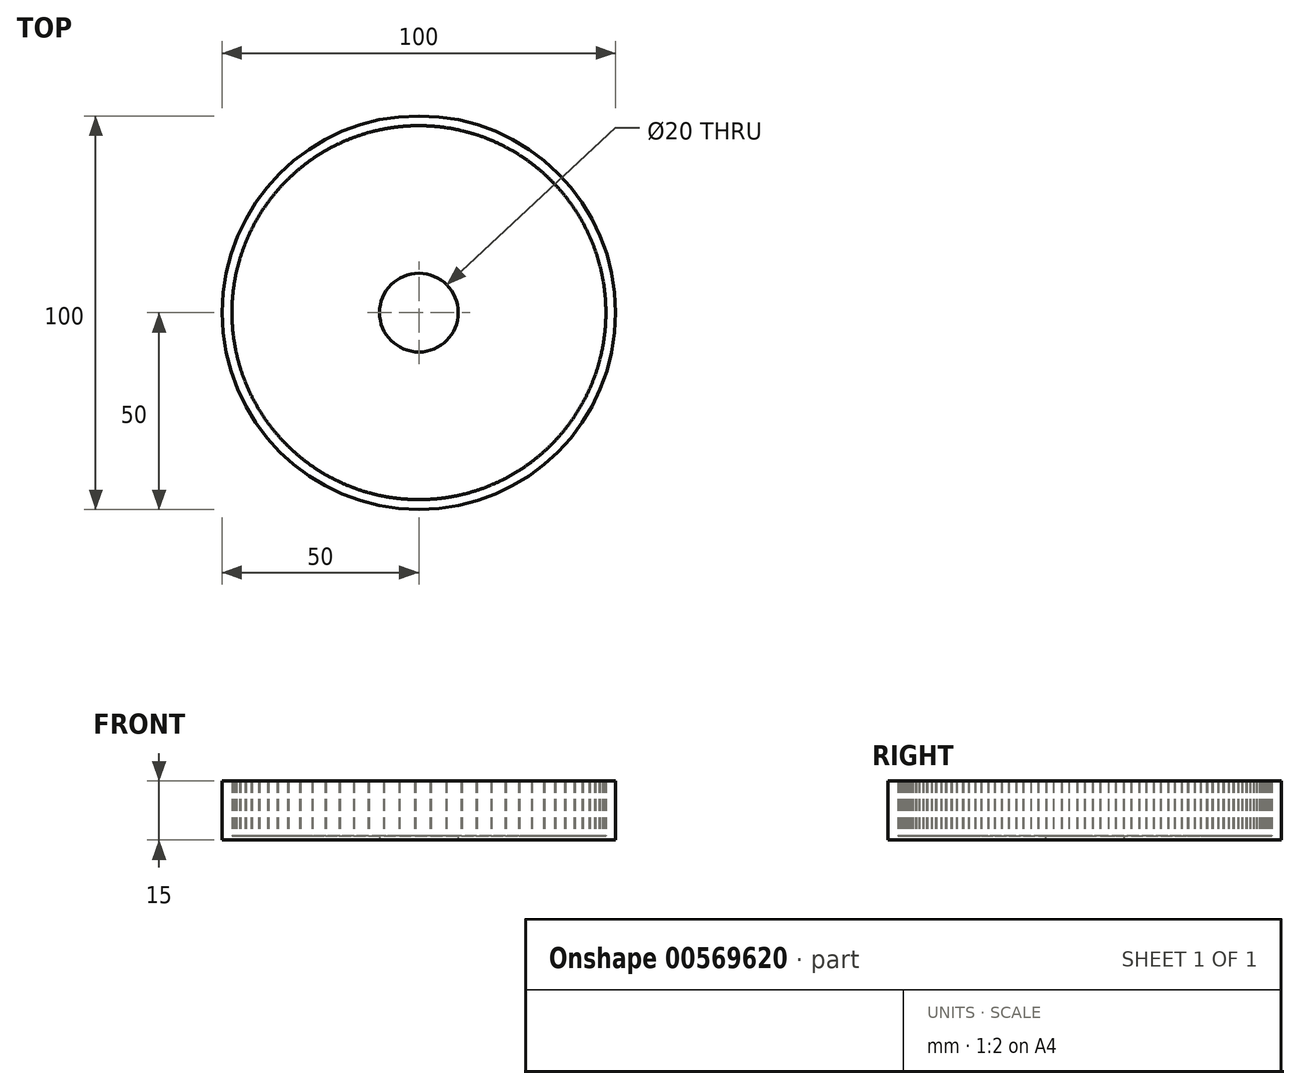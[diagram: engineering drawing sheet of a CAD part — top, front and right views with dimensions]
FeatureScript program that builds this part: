
annotation { "Feature Type Name" : "Feature", "Feature Type Description" : "" }
export const myFeature = defineFeature(function(context is Context, id is Id, definition is map)
    precondition{}
    {
        {
            var Q0;
            Q0=qCreatedBy(makeId("Top.planeOp"),FACE);
            var sketch = newSketch(context, id + "F0", { "sketchPlane" : qUnion([Q0])});
            skCircle(sketch, "E0", {"center": v(0, 0) * mm, "radius": 50 * mm});
            skCircle(sketch, "E1", {"center": v(0, 0) * mm, "radius": 10 * mm});
            skCircle(sketch, "E2", {"center": v(0, 0) * mm, "radius": 47.5 * mm});
            skLineSegment(sketch, "E3", {"start": v(47.5, 0) * mm, "end": v(47.3, -0.05) * mm});
            skLineSegment(sketch, "E4", {"start": v(47.3, -0.05) * mm, "end": v(47.5, -0.1) * mm});
            skLineSegment(sketch, "E5.1.0", {"start": v(47.33, 3.97) * mm, "end": v(47.14, 3.9) * mm});
            skLineSegment(sketch, "E5.1.1", {"start": v(47.14, 3.9) * mm, "end": v(47.34, 3.88) * mm});
            skLineSegment(sketch, "E5.2.0", {"start": v(46.83, 7.92) * mm, "end": v(46.65, 7.84) * mm});
            skLineSegment(sketch, "E5.2.1", {"start": v(46.65, 7.84) * mm, "end": v(46.85, 7.82) * mm});
            skLineSegment(sketch, "E6.2.3.0", {"start": v(46, 11.81) * mm, "end": v(45.83, 11.71) * mm});
            skLineSegment(sketch, "E6.3.3.0", {"start": v(45.83, 11.71) * mm, "end": v(46.03, 11.72) * mm});
            skLineSegment(sketch, "E6.2.4.0", {"start": v(44.86, 15.62) * mm, "end": v(44.69, 15.5) * mm});
            skLineSegment(sketch, "E6.3.4.0", {"start": v(44.69, 15.5) * mm, "end": v(44.9, 15.53) * mm});
            skLineSegment(sketch, "E6.2.5.0", {"start": v(43.4, 19.32) * mm, "end": v(43.23, 19.2) * mm});
            skLineSegment(sketch, "E6.3.5.0", {"start": v(43.23, 19.2) * mm, "end": v(43.43, 19.23) * mm});
            skLineSegment(sketch, "E6.2.6.0", {"start": v(41.62, 22.88) * mm, "end": v(41.47, 22.74) * mm});
            skLineSegment(sketch, "E6.3.6.0", {"start": v(41.47, 22.74) * mm, "end": v(41.67, 22.8) * mm});
            skLineSegment(sketch, "E6.2.7.0", {"start": v(39.56, 26.29) * mm, "end": v(39.42, 26.13) * mm});
            skLineSegment(sketch, "E6.3.7.0", {"start": v(39.42, 26.13) * mm, "end": v(39.62, 26.2) * mm});
            skLineSegment(sketch, "E6.2.8.0", {"start": v(37.23, 29.5) * mm, "end": v(37.1, 29.34) * mm});
            skLineSegment(sketch, "E6.3.8.0", {"start": v(37.1, 29.34) * mm, "end": v(37.29, 29.43) * mm});
            skLineSegment(sketch, "E6.2.9.0", {"start": v(34.63, 32.52) * mm, "end": v(34.51, 32.34) * mm});
            skLineSegment(sketch, "E6.3.9.0", {"start": v(34.51, 32.34) * mm, "end": v(34.7, 32.44) * mm});
            skLineSegment(sketch, "E6.2.10.0", {"start": v(31.78, 35.3) * mm, "end": v(31.69, 35.12) * mm});
            skLineSegment(sketch, "E6.3.10.0", {"start": v(31.69, 35.12) * mm, "end": v(31.86, 35.23) * mm});
            skLineSegment(sketch, "E6.2.11.0", {"start": v(28.72, 37.84) * mm, "end": v(28.64, 37.65) * mm});
            skLineSegment(sketch, "E6.3.11.0", {"start": v(28.64, 37.65) * mm, "end": v(28.8, 37.77) * mm});
            skLineSegment(sketch, "E6.2.12.0", {"start": v(25.45, 40.1) * mm, "end": v(25.39, 39.9) * mm});
            skLineSegment(sketch, "E6.3.12.0", {"start": v(25.39, 39.9) * mm, "end": v(25.54, 40.05) * mm});
            skLineSegment(sketch, "E6.2.13.0", {"start": v(22, 42.1) * mm, "end": v(21.96, 41.9) * mm});
            skLineSegment(sketch, "E6.3.13.0", {"start": v(21.96, 41.9) * mm, "end": v(22.1, 42.05) * mm});
            skLineSegment(sketch, "E6.2.14.0", {"start": v(18.4, 43.79) * mm, "end": v(18.38, 43.58) * mm});
            skLineSegment(sketch, "E6.3.14.0", {"start": v(18.38, 43.58) * mm, "end": v(18.5, 43.75) * mm});
            skLineSegment(sketch, "E6.2.15.0", {"start": v(14.68, 45.18) * mm, "end": v(14.66, 44.97) * mm});
            skLineSegment(sketch, "E6.3.15.0", {"start": v(14.66, 44.97) * mm, "end": v(14.77, 45.14) * mm});
            skLineSegment(sketch, "E6.2.16.0", {"start": v(10.85, 46.24) * mm, "end": v(10.85, 46.04) * mm});
            skLineSegment(sketch, "E6.3.16.0", {"start": v(10.85, 46.04) * mm, "end": v(10.94, 46.22) * mm});
            skLineSegment(sketch, "E6.2.17.0", {"start": v(6.94, 47) * mm, "end": v(6.96, 46.79) * mm});
            skLineSegment(sketch, "E6.3.17.0", {"start": v(6.96, 46.79) * mm, "end": v(7.04, 46.98) * mm});
            skLineSegment(sketch, "E6.2.18.0", {"start": v(2.98, 47.4) * mm, "end": v(3.02, 47.2) * mm});
            skLineSegment(sketch, "E6.3.18.0", {"start": v(3.02, 47.2) * mm, "end": v(3.08, 47.4) * mm});
            skLineSegment(sketch, "E6.2.19.0", {"start": v(-1, 47.49) * mm, "end": v(-0.94, 47.3) * mm});
            skLineSegment(sketch, "E6.3.19.0", {"start": v(-0.94, 47.3) * mm, "end": v(-0.9, 47.5) * mm});
            skLineSegment(sketch, "E6.2.20.0", {"start": v(-4.97, 47.24) * mm, "end": v(-4.9, 47.05) * mm});
            skLineSegment(sketch, "E6.3.20.0", {"start": v(-4.9, 47.05) * mm, "end": v(-4.87, 47.25) * mm});
            skLineSegment(sketch, "E6.2.21.0", {"start": v(-8.9, 46.66) * mm, "end": v(-8.81, 46.47) * mm});
            skLineSegment(sketch, "E6.3.21.0", {"start": v(-8.81, 46.47) * mm, "end": v(-8.8, 46.68) * mm});
            skLineSegment(sketch, "E6.2.22.0", {"start": v(-12.77, 45.75) * mm, "end": v(-12.67, 45.57) * mm});
            skLineSegment(sketch, "E6.3.22.0", {"start": v(-12.67, 45.57) * mm, "end": v(-12.68, 45.78) * mm});
            skLineSegment(sketch, "E6.2.23.0", {"start": v(-16.56, 44.52) * mm, "end": v(-16.44, 44.35) * mm});
            skLineSegment(sketch, "E6.3.23.0", {"start": v(-16.44, 44.35) * mm, "end": v(-16.46, 44.56) * mm});
            skLineSegment(sketch, "E6.2.24.0", {"start": v(-20.22, 42.98) * mm, "end": v(-20.1, 42.82) * mm});
            skLineSegment(sketch, "E6.3.24.0", {"start": v(-20.1, 42.82) * mm, "end": v(-20.13, 43.02) * mm});
            skLineSegment(sketch, "E6.2.25.0", {"start": v(-23.75, 41.14) * mm, "end": v(-23.6, 40.99) * mm});
            skLineSegment(sketch, "E6.3.25.0", {"start": v(-23.6, 40.99) * mm, "end": v(-23.66, 41.19) * mm});
            skLineSegment(sketch, "E6.2.26.0", {"start": v(-27.1, 39) * mm, "end": v(-26.95, 38.87) * mm});
            skLineSegment(sketch, "E6.3.26.0", {"start": v(-26.95, 38.87) * mm, "end": v(-27.03, 39.06) * mm});
            skLineSegment(sketch, "E6.2.27.0", {"start": v(-30.28, 36.6) * mm, "end": v(-30.11, 36.48) * mm});
            skLineSegment(sketch, "E6.3.27.0", {"start": v(-30.11, 36.48) * mm, "end": v(-30.2, 36.66) * mm});
            skLineSegment(sketch, "E6.2.28.0", {"start": v(-33.23, 33.94) * mm, "end": v(-33.06, 33.83) * mm});
            skLineSegment(sketch, "E6.3.28.0", {"start": v(-33.06, 33.83) * mm, "end": v(-33.16, 34) * mm});
            skLineSegment(sketch, "E6.2.29.0", {"start": v(-35.96, 31.04) * mm, "end": v(-35.77, 30.94) * mm});
            skLineSegment(sketch, "E6.3.29.0", {"start": v(-35.77, 30.94) * mm, "end": v(-35.9, 31.11) * mm});
            skLineSegment(sketch, "E6.2.30.0", {"start": v(-38.43, 27.92) * mm, "end": v(-38.24, 27.84) * mm});
            skLineSegment(sketch, "E6.3.30.0", {"start": v(-38.24, 27.84) * mm, "end": v(-38.37, 28) * mm});
            skLineSegment(sketch, "E6.2.31.0", {"start": v(-40.63, 24.6) * mm, "end": v(-40.43, 24.55) * mm});
            skLineSegment(sketch, "E6.3.31.0", {"start": v(-40.43, 24.55) * mm, "end": v(-40.58, 24.7) * mm});
            skLineSegment(sketch, "E6.2.32.0", {"start": v(-42.55, 21.12) * mm, "end": v(-42.34, 21.08) * mm});
            skLineSegment(sketch, "E6.3.32.0", {"start": v(-42.34, 21.08) * mm, "end": v(-42.5, 21.2) * mm});
            skLineSegment(sketch, "E6.2.33.0", {"start": v(-44.16, 17.49) * mm, "end": v(-43.96, 17.46) * mm});
            skLineSegment(sketch, "E6.3.33.0", {"start": v(-43.96, 17.46) * mm, "end": v(-44.13, 17.58) * mm});
            skLineSegment(sketch, "E6.2.34.0", {"start": v(-45.47, 13.73) * mm, "end": v(-45.27, 13.72) * mm});
            skLineSegment(sketch, "E6.3.34.0", {"start": v(-45.27, 13.72) * mm, "end": v(-45.44, 13.82) * mm});
            skLineSegment(sketch, "E6.2.35.0", {"start": v(-46.46, 9.88) * mm, "end": v(-46.26, 9.88) * mm});
            skLineSegment(sketch, "E6.3.35.0", {"start": v(-46.26, 9.88) * mm, "end": v(-46.44, 9.97) * mm});
            skLineSegment(sketch, "E6.2.36.0", {"start": v(-47.13, 5.95) * mm, "end": v(-46.92, 5.98) * mm});
            skLineSegment(sketch, "E6.3.36.0", {"start": v(-46.92, 5.98) * mm, "end": v(-47.11, 6.05) * mm});
            skLineSegment(sketch, "E6.2.37.0", {"start": v(-47.46, 1.99) * mm, "end": v(-47.26, 2.03) * mm});
            skLineSegment(sketch, "E6.3.37.0", {"start": v(-47.26, 2.03) * mm, "end": v(-47.45, 2.09) * mm});
            skLineSegment(sketch, "E6.2.38.0", {"start": v(-47.46, -1.99) * mm, "end": v(-47.26, -1.93) * mm});
            skLineSegment(sketch, "E6.3.38.0", {"start": v(-47.26, -1.93) * mm, "end": v(-47.46, -1.89) * mm});
            skLineSegment(sketch, "E6.2.39.0", {"start": v(-47.13, -5.95) * mm, "end": v(-46.93, -5.88) * mm});
            skLineSegment(sketch, "E6.3.39.0", {"start": v(-46.93, -5.88) * mm, "end": v(-47.14, -5.85) * mm});
            skLineSegment(sketch, "E6.2.40.0", {"start": v(-46.46, -9.88) * mm, "end": v(-46.28, -9.79) * mm});
            skLineSegment(sketch, "E6.3.40.0", {"start": v(-46.28, -9.79) * mm, "end": v(-46.48, -9.78) * mm});
            skLineSegment(sketch, "E6.2.41.0", {"start": v(-45.47, -13.73) * mm, "end": v(-45.3, -13.62) * mm});
            skLineSegment(sketch, "E6.3.41.0", {"start": v(-45.3, -13.62) * mm, "end": v(-45.5, -13.63) * mm});
            skLineSegment(sketch, "E6.2.42.0", {"start": v(-44.16, -17.49) * mm, "end": v(-44, -17.37) * mm});
            skLineSegment(sketch, "E6.3.42.0", {"start": v(-44, -17.37) * mm, "end": v(-44.2, -17.4) * mm});
            skLineSegment(sketch, "E6.2.43.0", {"start": v(-42.55, -21.12) * mm, "end": v(-42.39, -20.99) * mm});
            skLineSegment(sketch, "E6.3.43.0", {"start": v(-42.39, -20.99) * mm, "end": v(-42.6, -21.03) * mm});
            skLineSegment(sketch, "E6.2.44.0", {"start": v(-40.63, -24.6) * mm, "end": v(-40.48, -24.46) * mm});
            skLineSegment(sketch, "E6.3.44.0", {"start": v(-40.48, -24.46) * mm, "end": v(-40.68, -24.52) * mm});
            skLineSegment(sketch, "E6.2.45.0", {"start": v(-38.43, -27.92) * mm, "end": v(-38.3, -27.76) * mm});
            skLineSegment(sketch, "E6.3.45.0", {"start": v(-38.3, -27.76) * mm, "end": v(-38.49, -27.84) * mm});
            skLineSegment(sketch, "E6.2.46.0", {"start": v(-35.96, -31.04) * mm, "end": v(-35.84, -30.87) * mm});
            skLineSegment(sketch, "E6.3.46.0", {"start": v(-35.84, -30.87) * mm, "end": v(-36.02, -30.96) * mm});
            skLineSegment(sketch, "E6.2.47.0", {"start": v(-33.23, -33.94) * mm, "end": v(-33.13, -33.76) * mm});
            skLineSegment(sketch, "E6.3.47.0", {"start": v(-33.13, -33.76) * mm, "end": v(-33.3, -33.87) * mm});
            skLineSegment(sketch, "E6.2.48.0", {"start": v(-30.28, -36.6) * mm, "end": v(-30.19, -36.41) * mm});
            skLineSegment(sketch, "E6.3.48.0", {"start": v(-30.19, -36.41) * mm, "end": v(-30.35, -36.54) * mm});
            skLineSegment(sketch, "E6.2.49.0", {"start": v(-27.1, -39) * mm, "end": v(-27.04, -38.81) * mm});
            skLineSegment(sketch, "E6.3.49.0", {"start": v(-27.04, -38.81) * mm, "end": v(-27.2, -38.95) * mm});
            skLineSegment(sketch, "E6.2.50.0", {"start": v(-23.75, -41.14) * mm, "end": v(-23.7, -40.94) * mm});
            skLineSegment(sketch, "E6.3.50.0", {"start": v(-23.7, -40.94) * mm, "end": v(-23.84, -41.09) * mm});
            skLineSegment(sketch, "E6.2.51.0", {"start": v(-20.22, -42.98) * mm, "end": v(-20.18, -42.78) * mm});
            skLineSegment(sketch, "E6.3.51.0", {"start": v(-20.18, -42.78) * mm, "end": v(-20.31, -42.94) * mm});
            skLineSegment(sketch, "E6.2.52.0", {"start": v(-16.56, -44.52) * mm, "end": v(-16.53, -44.32) * mm});
            skLineSegment(sketch, "E6.3.52.0", {"start": v(-16.53, -44.32) * mm, "end": v(-16.65, -44.49) * mm});
            skLineSegment(sketch, "E6.2.53.0", {"start": v(-12.77, -45.75) * mm, "end": v(-12.77, -45.54) * mm});
            skLineSegment(sketch, "E6.3.53.0", {"start": v(-12.77, -45.54) * mm, "end": v(-12.87, -45.72) * mm});
            skLineSegment(sketch, "E6.2.54.0", {"start": v(-8.9, -46.66) * mm, "end": v(-8.91, -46.45) * mm});
            skLineSegment(sketch, "E6.3.54.0", {"start": v(-8.91, -46.45) * mm, "end": v(-9, -46.64) * mm});
            skLineSegment(sketch, "E6.2.55.0", {"start": v(-4.97, -47.24) * mm, "end": v(-5, -47.04) * mm});
            skLineSegment(sketch, "E6.3.55.0", {"start": v(-5, -47.04) * mm, "end": v(-5.06, -47.23) * mm});
            skLineSegment(sketch, "E6.2.56.0", {"start": v(-1, -47.49) * mm, "end": v(-1.04, -47.29) * mm});
            skLineSegment(sketch, "E6.3.56.0", {"start": v(-1.04, -47.29) * mm, "end": v(-1.1, -47.49) * mm});
            skLineSegment(sketch, "E6.2.57.0", {"start": v(2.98, -47.4) * mm, "end": v(2.92, -47.2) * mm});
            skLineSegment(sketch, "E6.3.57.0", {"start": v(2.92, -47.2) * mm, "end": v(2.88, -47.41) * mm});
            skLineSegment(sketch, "E6.2.58.0", {"start": v(6.94, -47) * mm, "end": v(6.86, -46.8) * mm});
            skLineSegment(sketch, "E6.3.58.0", {"start": v(6.86, -46.8) * mm, "end": v(6.84, -47) * mm});
            skLineSegment(sketch, "E6.2.59.0", {"start": v(10.85, -46.24) * mm, "end": v(10.75, -46.06) * mm});
            skLineSegment(sketch, "E6.3.59.0", {"start": v(10.75, -46.06) * mm, "end": v(10.75, -46.27) * mm});
            skLineSegment(sketch, "E6.2.60.0", {"start": v(14.68, -45.18) * mm, "end": v(14.57, -45) * mm});
            skLineSegment(sketch, "E6.3.60.0", {"start": v(14.57, -45) * mm, "end": v(14.58, -45.2) * mm});
            skLineSegment(sketch, "E6.2.61.0", {"start": v(18.4, -43.79) * mm, "end": v(18.28, -43.62) * mm});
            skLineSegment(sketch, "E6.3.61.0", {"start": v(18.28, -43.62) * mm, "end": v(18.31, -43.83) * mm});
            skLineSegment(sketch, "E6.2.62.0", {"start": v(22, -42.1) * mm, "end": v(21.87, -41.94) * mm});
            skLineSegment(sketch, "E6.3.62.0", {"start": v(21.87, -41.94) * mm, "end": v(21.92, -42.14) * mm});
            skLineSegment(sketch, "E6.2.63.0", {"start": v(25.45, -40.1) * mm, "end": v(25.3, -39.96) * mm});
            skLineSegment(sketch, "E6.3.63.0", {"start": v(25.3, -39.96) * mm, "end": v(25.37, -40.16) * mm});
            skLineSegment(sketch, "E6.2.64.0", {"start": v(28.72, -37.84) * mm, "end": v(28.56, -37.7) * mm});
            skLineSegment(sketch, "E6.3.64.0", {"start": v(28.56, -37.7) * mm, "end": v(28.64, -37.9) * mm});
            skLineSegment(sketch, "E6.2.65.0", {"start": v(31.78, -35.3) * mm, "end": v(31.61, -35.18) * mm});
            skLineSegment(sketch, "E6.3.65.0", {"start": v(31.61, -35.18) * mm, "end": v(31.7, -35.37) * mm});
            skLineSegment(sketch, "E6.2.66.0", {"start": v(34.63, -32.52) * mm, "end": v(34.45, -32.42) * mm});
            skLineSegment(sketch, "E6.3.66.0", {"start": v(34.45, -32.42) * mm, "end": v(34.56, -32.59) * mm});
            skLineSegment(sketch, "E6.2.67.0", {"start": v(37.23, -29.5) * mm, "end": v(37.04, -29.42) * mm});
            skLineSegment(sketch, "E6.3.67.0", {"start": v(37.04, -29.42) * mm, "end": v(37.16, -29.58) * mm});
            skLineSegment(sketch, "E6.2.68.0", {"start": v(39.56, -26.29) * mm, "end": v(39.37, -26.22) * mm});
            skLineSegment(sketch, "E6.3.68.0", {"start": v(39.37, -26.22) * mm, "end": v(39.5, -26.37) * mm});
            skLineSegment(sketch, "E6.2.69.0", {"start": v(41.62, -22.88) * mm, "end": v(41.43, -22.83) * mm});
            skLineSegment(sketch, "E6.3.69.0", {"start": v(41.43, -22.83) * mm, "end": v(41.58, -22.97) * mm});
            skLineSegment(sketch, "E6.2.70.0", {"start": v(43.4, -19.32) * mm, "end": v(43.2, -19.28) * mm});
            skLineSegment(sketch, "E6.3.70.0", {"start": v(43.2, -19.28) * mm, "end": v(43.35, -19.41) * mm});
            skLineSegment(sketch, "E6.2.71.0", {"start": v(44.86, -15.62) * mm, "end": v(44.65, -15.6) * mm});
            skLineSegment(sketch, "E6.3.71.0", {"start": v(44.65, -15.6) * mm, "end": v(44.82, -15.72) * mm});
            skLineSegment(sketch, "E6.2.72.0", {"start": v(46, -11.81) * mm, "end": v(45.8, -11.81) * mm});
            skLineSegment(sketch, "E6.3.72.0", {"start": v(45.8, -11.81) * mm, "end": v(45.98, -11.9) * mm});
            skLineSegment(sketch, "E6.2.73.0", {"start": v(46.83, -7.92) * mm, "end": v(46.63, -7.94) * mm});
            skLineSegment(sketch, "E6.3.73.0", {"start": v(46.63, -7.94) * mm, "end": v(46.82, -8.02) * mm});
            skLineSegment(sketch, "E6.2.74.0", {"start": v(47.33, -3.97) * mm, "end": v(47.13, -4) * mm});
            skLineSegment(sketch, "E6.3.74.0", {"start": v(47.13, -4) * mm, "end": v(47.32, -4.07) * mm});
            skSolve(sketch);
        }
        {
            var Q0;
            Q0=makeQuery(id+"F0.imprint","IMPRINT",FACE,{"disambiguationData":[TD([[makeQuery(id+"F0.imprint","IMPRINT",EDGE,{"derivedFrom":sQuery(id+"F0.wireOp",EDGE,"E0")}),1.0]])]});
            var Q1;
            {var subQ0=sQuery(id+"F0.wireOp",EDGE,"E6.2.40.0");Q1=makeQuery(id+"F0.imprint","IMPRINT",FACE,{"disambiguationData":[TD([[makeQuery(id+"F0.imprint","IMPRINT",EDGE,{"derivedFrom":subQ0}),1.0]])]});}
            var Q2;
            {var subQ0=sQuery(id+"F0.wireOp",EDGE,"E6.2.72.0");Q2=makeQuery(id+"F0.imprint","IMPRINT",FACE,{"disambiguationData":[TD([[makeQuery(id+"F0.imprint","IMPRINT",EDGE,{"derivedFrom":subQ0}),1.0]])]});}
            var Q3;
            {var subQ0=sQuery(id+"F0.wireOp",EDGE,"E6.2.44.0");Q3=makeQuery(id+"F0.imprint","IMPRINT",FACE,{"disambiguationData":[TD([[makeQuery(id+"F0.imprint","IMPRINT",EDGE,{"derivedFrom":subQ0}),1.0]])]});}
            var Q4;
            {var subQ0=sQuery(id+"F0.wireOp",EDGE,"E6.2.10.0");Q4=makeQuery(id+"F0.imprint","IMPRINT",FACE,{"disambiguationData":[TD([[makeQuery(id+"F0.imprint","IMPRINT",EDGE,{"derivedFrom":subQ0}),1.0]])]});}
            var Q5;
            {var subQ0=sQuery(id+"F0.wireOp",EDGE,"E6.2.26.0");Q5=makeQuery(id+"F0.imprint","IMPRINT",FACE,{"disambiguationData":[TD([[makeQuery(id+"F0.imprint","IMPRINT",EDGE,{"derivedFrom":subQ0}),1.0]])]});}
            var Q6;
            {var subQ0=sQuery(id+"F0.wireOp",EDGE,"E6.2.56.0");Q6=makeQuery(id+"F0.imprint","IMPRINT",FACE,{"disambiguationData":[TD([[makeQuery(id+"F0.imprint","IMPRINT",EDGE,{"derivedFrom":subQ0}),1.0]])]});}
            var Q7;
            {var subQ0=sQuery(id+"F0.wireOp",EDGE,"E6.2.37.0");Q7=makeQuery(id+"F0.imprint","IMPRINT",FACE,{"disambiguationData":[TD([[makeQuery(id+"F0.imprint","IMPRINT",EDGE,{"derivedFrom":subQ0}),1.0]])]});}
            var Q8;
            {var subQ0=sQuery(id+"F0.wireOp",EDGE,"E6.2.33.0");Q8=makeQuery(id+"F0.imprint","IMPRINT",FACE,{"disambiguationData":[TD([[makeQuery(id+"F0.imprint","IMPRINT",EDGE,{"derivedFrom":subQ0}),1.0]])]});}
            var Q9;
            {var subQ0=sQuery(id+"F0.wireOp",EDGE,"E6.2.49.0");Q9=makeQuery(id+"F0.imprint","IMPRINT",FACE,{"disambiguationData":[TD([[makeQuery(id+"F0.imprint","IMPRINT",EDGE,{"derivedFrom":subQ0}),1.0]])]});}
            var Q10;
            {var subQ0=sQuery(id+"F0.wireOp",EDGE,"E6.2.60.0");Q10=makeQuery(id+"F0.imprint","IMPRINT",FACE,{"disambiguationData":[TD([[makeQuery(id+"F0.imprint","IMPRINT",EDGE,{"derivedFrom":subQ0}),1.0]])]});}
            var Q11;
            {var subQ0=sQuery(id+"F0.wireOp",EDGE,"E6.2.28.0");Q11=makeQuery(id+"F0.imprint","IMPRINT",FACE,{"disambiguationData":[TD([[makeQuery(id+"F0.imprint","IMPRINT",EDGE,{"derivedFrom":subQ0}),1.0]])]});}
            var Q12;
            {var subQ0=sQuery(id+"F0.wireOp",EDGE,"E6.2.23.0");Q12=makeQuery(id+"F0.imprint","IMPRINT",FACE,{"disambiguationData":[TD([[makeQuery(id+"F0.imprint","IMPRINT",EDGE,{"derivedFrom":subQ0}),1.0]])]});}
            var Q13;
            {var subQ0=sQuery(id+"F0.wireOp",EDGE,"E6.2.3.0");Q13=makeQuery(id+"F0.imprint","IMPRINT",FACE,{"disambiguationData":[TD([[makeQuery(id+"F0.imprint","IMPRINT",EDGE,{"derivedFrom":subQ0}),1.0]])]});}
            var Q14;
            {var subQ0=sQuery(id+"F0.wireOp",EDGE,"E6.2.71.0");Q14=makeQuery(id+"F0.imprint","IMPRINT",FACE,{"disambiguationData":[TD([[makeQuery(id+"F0.imprint","IMPRINT",EDGE,{"derivedFrom":subQ0}),1.0]])]});}
            var Q15;
            {var subQ0=sQuery(id+"F0.wireOp",EDGE,"E6.2.22.0");Q15=makeQuery(id+"F0.imprint","IMPRINT",FACE,{"disambiguationData":[TD([[makeQuery(id+"F0.imprint","IMPRINT",EDGE,{"derivedFrom":subQ0}),1.0]])]});}
            var Q16;
            {var subQ0=sQuery(id+"F0.wireOp",EDGE,"E5.2.0");Q16=makeQuery(id+"F0.imprint","IMPRINT",FACE,{"disambiguationData":[TD([[makeQuery(id+"F0.imprint","IMPRINT",EDGE,{"derivedFrom":subQ0}),1.0]])]});}
            var Q17;
            {var subQ0=sQuery(id+"F0.wireOp",EDGE,"E6.2.24.0");Q17=makeQuery(id+"F0.imprint","IMPRINT",FACE,{"disambiguationData":[TD([[makeQuery(id+"F0.imprint","IMPRINT",EDGE,{"derivedFrom":subQ0}),1.0]])]});}
            var Q18;
            {var subQ0=sQuery(id+"F0.wireOp",EDGE,"E5.1.0");Q18=makeQuery(id+"F0.imprint","IMPRINT",FACE,{"disambiguationData":[TD([[makeQuery(id+"F0.imprint","IMPRINT",EDGE,{"derivedFrom":subQ0}),1.0]])]});}
            var Q19;
            {var subQ0=sQuery(id+"F0.wireOp",EDGE,"E6.2.55.0");Q19=makeQuery(id+"F0.imprint","IMPRINT",FACE,{"disambiguationData":[TD([[makeQuery(id+"F0.imprint","IMPRINT",EDGE,{"derivedFrom":subQ0}),1.0]])]});}
            var Q20;
            {var subQ0=sQuery(id+"F0.wireOp",EDGE,"E6.2.65.0");Q20=makeQuery(id+"F0.imprint","IMPRINT",FACE,{"disambiguationData":[TD([[makeQuery(id+"F0.imprint","IMPRINT",EDGE,{"derivedFrom":subQ0}),1.0]])]});}
            var Q21;
            {var subQ0=sQuery(id+"F0.wireOp",EDGE,"E6.2.17.0");Q21=makeQuery(id+"F0.imprint","IMPRINT",FACE,{"disambiguationData":[TD([[makeQuery(id+"F0.imprint","IMPRINT",EDGE,{"derivedFrom":subQ0}),1.0]])]});}
            var Q22;
            {var subQ0=sQuery(id+"F0.wireOp",EDGE,"E6.2.31.0");Q22=makeQuery(id+"F0.imprint","IMPRINT",FACE,{"disambiguationData":[TD([[makeQuery(id+"F0.imprint","IMPRINT",EDGE,{"derivedFrom":subQ0}),1.0]])]});}
            var Q23;
            {var subQ0=sQuery(id+"F0.wireOp",EDGE,"E6.2.57.0");Q23=makeQuery(id+"F0.imprint","IMPRINT",FACE,{"disambiguationData":[TD([[makeQuery(id+"F0.imprint","IMPRINT",EDGE,{"derivedFrom":subQ0}),1.0]])]});}
            var Q24;
            {var subQ0=sQuery(id+"F0.wireOp",EDGE,"E6.2.25.0");Q24=makeQuery(id+"F0.imprint","IMPRINT",FACE,{"disambiguationData":[TD([[makeQuery(id+"F0.imprint","IMPRINT",EDGE,{"derivedFrom":subQ0}),1.0]])]});}
            var Q25;
            {var subQ0=sQuery(id+"F0.wireOp",EDGE,"E6.2.74.0");Q25=makeQuery(id+"F0.imprint","IMPRINT",FACE,{"disambiguationData":[TD([[makeQuery(id+"F0.imprint","IMPRINT",EDGE,{"derivedFrom":subQ0}),1.0]])]});}
            var Q26;
            {var subQ0=sQuery(id+"F0.wireOp",EDGE,"E6.2.63.0");Q26=makeQuery(id+"F0.imprint","IMPRINT",FACE,{"disambiguationData":[TD([[makeQuery(id+"F0.imprint","IMPRINT",EDGE,{"derivedFrom":subQ0}),1.0]])]});}
            var Q27;
            {var subQ0=sQuery(id+"F0.wireOp",EDGE,"E6.2.47.0");Q27=makeQuery(id+"F0.imprint","IMPRINT",FACE,{"disambiguationData":[TD([[makeQuery(id+"F0.imprint","IMPRINT",EDGE,{"derivedFrom":subQ0}),1.0]])]});}
            var Q28;
            {var subQ0=sQuery(id+"F0.wireOp",EDGE,"E6.2.30.0");Q28=makeQuery(id+"F0.imprint","IMPRINT",FACE,{"disambiguationData":[TD([[makeQuery(id+"F0.imprint","IMPRINT",EDGE,{"derivedFrom":subQ0}),1.0]])]});}
            var Q29;
            {var subQ0=sQuery(id+"F0.wireOp",EDGE,"E6.2.12.0");Q29=makeQuery(id+"F0.imprint","IMPRINT",FACE,{"disambiguationData":[TD([[makeQuery(id+"F0.imprint","IMPRINT",EDGE,{"derivedFrom":subQ0}),1.0]])]});}
            var Q30;
            {var subQ0=sQuery(id+"F0.wireOp",EDGE,"E6.2.11.0");Q30=makeQuery(id+"F0.imprint","IMPRINT",FACE,{"disambiguationData":[TD([[makeQuery(id+"F0.imprint","IMPRINT",EDGE,{"derivedFrom":subQ0}),1.0]])]});}
            var Q31;
            {var subQ0=sQuery(id+"F0.wireOp",EDGE,"E6.2.9.0");Q31=makeQuery(id+"F0.imprint","IMPRINT",FACE,{"disambiguationData":[TD([[makeQuery(id+"F0.imprint","IMPRINT",EDGE,{"derivedFrom":subQ0}),1.0]])]});}
            var Q32;
            {var subQ0=sQuery(id+"F0.wireOp",EDGE,"E6.2.62.0");Q32=makeQuery(id+"F0.imprint","IMPRINT",FACE,{"disambiguationData":[TD([[makeQuery(id+"F0.imprint","IMPRINT",EDGE,{"derivedFrom":subQ0}),1.0]])]});}
            var Q33;
            {var subQ0=sQuery(id+"F0.wireOp",EDGE,"E6.2.35.0");Q33=makeQuery(id+"F0.imprint","IMPRINT",FACE,{"disambiguationData":[TD([[makeQuery(id+"F0.imprint","IMPRINT",EDGE,{"derivedFrom":subQ0}),1.0]])]});}
            var Q34;
            {var subQ0=sQuery(id+"F0.wireOp",EDGE,"E6.2.73.0");Q34=makeQuery(id+"F0.imprint","IMPRINT",FACE,{"disambiguationData":[TD([[makeQuery(id+"F0.imprint","IMPRINT",EDGE,{"derivedFrom":subQ0}),1.0]])]});}
            var Q35;
            {var subQ0=sQuery(id+"F0.wireOp",EDGE,"E3");Q35=makeQuery(id+"F0.imprint","IMPRINT",FACE,{"disambiguationData":[TD([[makeQuery(id+"F0.imprint","IMPRINT",EDGE,{"derivedFrom":subQ0}),1.0]])]});}
            var Q36;
            {var subQ0=sQuery(id+"F0.wireOp",EDGE,"E6.2.51.0");Q36=makeQuery(id+"F0.imprint","IMPRINT",FACE,{"disambiguationData":[TD([[makeQuery(id+"F0.imprint","IMPRINT",EDGE,{"derivedFrom":subQ0}),1.0]])]});}
            var Q37;
            {var subQ0=sQuery(id+"F0.wireOp",EDGE,"E6.2.14.0");Q37=makeQuery(id+"F0.imprint","IMPRINT",FACE,{"disambiguationData":[TD([[makeQuery(id+"F0.imprint","IMPRINT",EDGE,{"derivedFrom":subQ0}),1.0]])]});}
            var Q38;
            {var subQ0=sQuery(id+"F0.wireOp",EDGE,"E6.2.67.0");Q38=makeQuery(id+"F0.imprint","IMPRINT",FACE,{"disambiguationData":[TD([[makeQuery(id+"F0.imprint","IMPRINT",EDGE,{"derivedFrom":subQ0}),1.0]])]});}
            var Q39;
            {var subQ0=sQuery(id+"F0.wireOp",EDGE,"E6.2.13.0");Q39=makeQuery(id+"F0.imprint","IMPRINT",FACE,{"disambiguationData":[TD([[makeQuery(id+"F0.imprint","IMPRINT",EDGE,{"derivedFrom":subQ0}),1.0]])]});}
            var Q40;
            {var subQ0=sQuery(id+"F0.wireOp",EDGE,"E6.2.58.0");Q40=makeQuery(id+"F0.imprint","IMPRINT",FACE,{"disambiguationData":[TD([[makeQuery(id+"F0.imprint","IMPRINT",EDGE,{"derivedFrom":subQ0}),1.0]])]});}
            var Q41;
            {var subQ0=sQuery(id+"F0.wireOp",EDGE,"E6.2.6.0");Q41=makeQuery(id+"F0.imprint","IMPRINT",FACE,{"disambiguationData":[TD([[makeQuery(id+"F0.imprint","IMPRINT",EDGE,{"derivedFrom":subQ0}),1.0]])]});}
            var Q42;
            {var subQ0=sQuery(id+"F0.wireOp",EDGE,"E6.2.29.0");Q42=makeQuery(id+"F0.imprint","IMPRINT",FACE,{"disambiguationData":[TD([[makeQuery(id+"F0.imprint","IMPRINT",EDGE,{"derivedFrom":subQ0}),1.0]])]});}
            var Q43;
            {var subQ0=sQuery(id+"F0.wireOp",EDGE,"E6.2.27.0");Q43=makeQuery(id+"F0.imprint","IMPRINT",FACE,{"disambiguationData":[TD([[makeQuery(id+"F0.imprint","IMPRINT",EDGE,{"derivedFrom":subQ0}),1.0]])]});}
            var Q44;
            {var subQ0=sQuery(id+"F0.wireOp",EDGE,"E6.2.43.0");Q44=makeQuery(id+"F0.imprint","IMPRINT",FACE,{"disambiguationData":[TD([[makeQuery(id+"F0.imprint","IMPRINT",EDGE,{"derivedFrom":subQ0}),1.0]])]});}
            var Q45;
            {var subQ0=sQuery(id+"F0.wireOp",EDGE,"E6.2.59.0");Q45=makeQuery(id+"F0.imprint","IMPRINT",FACE,{"disambiguationData":[TD([[makeQuery(id+"F0.imprint","IMPRINT",EDGE,{"derivedFrom":subQ0}),1.0]])]});}
            var Q46;
            {var subQ0=sQuery(id+"F0.wireOp",EDGE,"E6.2.32.0");Q46=makeQuery(id+"F0.imprint","IMPRINT",FACE,{"disambiguationData":[TD([[makeQuery(id+"F0.imprint","IMPRINT",EDGE,{"derivedFrom":subQ0}),1.0]])]});}
            var Q47;
            {var subQ0=sQuery(id+"F0.wireOp",EDGE,"E6.2.7.0");Q47=makeQuery(id+"F0.imprint","IMPRINT",FACE,{"disambiguationData":[TD([[makeQuery(id+"F0.imprint","IMPRINT",EDGE,{"derivedFrom":subQ0}),1.0]])]});}
            var Q48;
            {var subQ0=sQuery(id+"F0.wireOp",EDGE,"E6.2.8.0");Q48=makeQuery(id+"F0.imprint","IMPRINT",FACE,{"disambiguationData":[TD([[makeQuery(id+"F0.imprint","IMPRINT",EDGE,{"derivedFrom":subQ0}),1.0]])]});}
            var Q49;
            {var subQ0=sQuery(id+"F0.wireOp",EDGE,"E6.2.48.0");Q49=makeQuery(id+"F0.imprint","IMPRINT",FACE,{"disambiguationData":[TD([[makeQuery(id+"F0.imprint","IMPRINT",EDGE,{"derivedFrom":subQ0}),1.0]])]});}
            var Q50;
            {var subQ0=sQuery(id+"F0.wireOp",EDGE,"E6.2.38.0");Q50=makeQuery(id+"F0.imprint","IMPRINT",FACE,{"disambiguationData":[TD([[makeQuery(id+"F0.imprint","IMPRINT",EDGE,{"derivedFrom":subQ0}),1.0]])]});}
            var Q51;
            {var subQ0=sQuery(id+"F0.wireOp",EDGE,"E6.2.39.0");Q51=makeQuery(id+"F0.imprint","IMPRINT",FACE,{"disambiguationData":[TD([[makeQuery(id+"F0.imprint","IMPRINT",EDGE,{"derivedFrom":subQ0}),1.0]])]});}
            var Q52;
            {var subQ0=sQuery(id+"F0.wireOp",EDGE,"E6.2.16.0");Q52=makeQuery(id+"F0.imprint","IMPRINT",FACE,{"disambiguationData":[TD([[makeQuery(id+"F0.imprint","IMPRINT",EDGE,{"derivedFrom":subQ0}),1.0]])]});}
            var Q53;
            {var subQ0=sQuery(id+"F0.wireOp",EDGE,"E6.2.19.0");Q53=makeQuery(id+"F0.imprint","IMPRINT",FACE,{"disambiguationData":[TD([[makeQuery(id+"F0.imprint","IMPRINT",EDGE,{"derivedFrom":subQ0}),1.0]])]});}
            var Q54;
            {var subQ0=sQuery(id+"F0.wireOp",EDGE,"E6.2.15.0");Q54=makeQuery(id+"F0.imprint","IMPRINT",FACE,{"disambiguationData":[TD([[makeQuery(id+"F0.imprint","IMPRINT",EDGE,{"derivedFrom":subQ0}),1.0]])]});}
            var Q55;
            {var subQ0=sQuery(id+"F0.wireOp",EDGE,"E6.2.18.0");Q55=makeQuery(id+"F0.imprint","IMPRINT",FACE,{"disambiguationData":[TD([[makeQuery(id+"F0.imprint","IMPRINT",EDGE,{"derivedFrom":subQ0}),1.0]])]});}
            var Q56;
            {var subQ0=sQuery(id+"F0.wireOp",EDGE,"E6.2.66.0");Q56=makeQuery(id+"F0.imprint","IMPRINT",FACE,{"disambiguationData":[TD([[makeQuery(id+"F0.imprint","IMPRINT",EDGE,{"derivedFrom":subQ0}),1.0]])]});}
            var Q57;
            {var subQ0=sQuery(id+"F0.wireOp",EDGE,"E6.2.50.0");Q57=makeQuery(id+"F0.imprint","IMPRINT",FACE,{"disambiguationData":[TD([[makeQuery(id+"F0.imprint","IMPRINT",EDGE,{"derivedFrom":subQ0}),1.0]])]});}
            var Q58;
            {var subQ0=sQuery(id+"F0.wireOp",EDGE,"E6.2.34.0");Q58=makeQuery(id+"F0.imprint","IMPRINT",FACE,{"disambiguationData":[TD([[makeQuery(id+"F0.imprint","IMPRINT",EDGE,{"derivedFrom":subQ0}),1.0]])]});}
            var Q59;
            {var subQ0=sQuery(id+"F0.wireOp",EDGE,"E6.2.20.0");Q59=makeQuery(id+"F0.imprint","IMPRINT",FACE,{"disambiguationData":[TD([[makeQuery(id+"F0.imprint","IMPRINT",EDGE,{"derivedFrom":subQ0}),1.0]])]});}
            var Q60;
            {var subQ0=sQuery(id+"F0.wireOp",EDGE,"E6.2.68.0");Q60=makeQuery(id+"F0.imprint","IMPRINT",FACE,{"disambiguationData":[TD([[makeQuery(id+"F0.imprint","IMPRINT",EDGE,{"derivedFrom":subQ0}),1.0]])]});}
            var Q61;
            {var subQ0=sQuery(id+"F0.wireOp",EDGE,"E6.2.52.0");Q61=makeQuery(id+"F0.imprint","IMPRINT",FACE,{"disambiguationData":[TD([[makeQuery(id+"F0.imprint","IMPRINT",EDGE,{"derivedFrom":subQ0}),1.0]])]});}
            var Q62;
            {var subQ0=sQuery(id+"F0.wireOp",EDGE,"E6.2.36.0");Q62=makeQuery(id+"F0.imprint","IMPRINT",FACE,{"disambiguationData":[TD([[makeQuery(id+"F0.imprint","IMPRINT",EDGE,{"derivedFrom":subQ0}),1.0]])]});}
            var Q63;
            {var subQ0=sQuery(id+"F0.wireOp",EDGE,"E6.2.70.0");Q63=makeQuery(id+"F0.imprint","IMPRINT",FACE,{"disambiguationData":[TD([[makeQuery(id+"F0.imprint","IMPRINT",EDGE,{"derivedFrom":subQ0}),1.0]])]});}
            var Q64;
            {var subQ0=sQuery(id+"F0.wireOp",EDGE,"E6.2.21.0");Q64=makeQuery(id+"F0.imprint","IMPRINT",FACE,{"disambiguationData":[TD([[makeQuery(id+"F0.imprint","IMPRINT",EDGE,{"derivedFrom":subQ0}),1.0]])]});}
            var Q65;
            {var subQ0=sQuery(id+"F0.wireOp",EDGE,"E6.2.69.0");Q65=makeQuery(id+"F0.imprint","IMPRINT",FACE,{"disambiguationData":[TD([[makeQuery(id+"F0.imprint","IMPRINT",EDGE,{"derivedFrom":subQ0}),1.0]])]});}
            var Q66;
            {var subQ0=sQuery(id+"F0.wireOp",EDGE,"E6.2.53.0");Q66=makeQuery(id+"F0.imprint","IMPRINT",FACE,{"disambiguationData":[TD([[makeQuery(id+"F0.imprint","IMPRINT",EDGE,{"derivedFrom":subQ0}),1.0]])]});}
            var Q67;
            {var subQ0=sQuery(id+"F0.wireOp",EDGE,"E6.2.54.0");Q67=makeQuery(id+"F0.imprint","IMPRINT",FACE,{"disambiguationData":[TD([[makeQuery(id+"F0.imprint","IMPRINT",EDGE,{"derivedFrom":subQ0}),1.0]])]});}
            var Q68;
            {var subQ0=sQuery(id+"F0.wireOp",EDGE,"E6.2.64.0");Q68=makeQuery(id+"F0.imprint","IMPRINT",FACE,{"disambiguationData":[TD([[makeQuery(id+"F0.imprint","IMPRINT",EDGE,{"derivedFrom":subQ0}),1.0]])]});}
            var Q69;
            {var subQ0=sQuery(id+"F0.wireOp",EDGE,"E6.2.46.0");Q69=makeQuery(id+"F0.imprint","IMPRINT",FACE,{"disambiguationData":[TD([[makeQuery(id+"F0.imprint","IMPRINT",EDGE,{"derivedFrom":subQ0}),1.0]])]});}
            var Q70;
            {var subQ0=sQuery(id+"F0.wireOp",EDGE,"E6.2.45.0");Q70=makeQuery(id+"F0.imprint","IMPRINT",FACE,{"disambiguationData":[TD([[makeQuery(id+"F0.imprint","IMPRINT",EDGE,{"derivedFrom":subQ0}),1.0]])]});}
            var Q71;
            {var subQ0=sQuery(id+"F0.wireOp",EDGE,"E6.2.5.0");Q71=makeQuery(id+"F0.imprint","IMPRINT",FACE,{"disambiguationData":[TD([[makeQuery(id+"F0.imprint","IMPRINT",EDGE,{"derivedFrom":subQ0}),1.0]])]});}
            var Q72;
            {var subQ0=sQuery(id+"F0.wireOp",EDGE,"E6.2.61.0");Q72=makeQuery(id+"F0.imprint","IMPRINT",FACE,{"disambiguationData":[TD([[makeQuery(id+"F0.imprint","IMPRINT",EDGE,{"derivedFrom":subQ0}),1.0]])]});}
            var Q73;
            {var subQ0=sQuery(id+"F0.wireOp",EDGE,"E6.2.4.0");Q73=makeQuery(id+"F0.imprint","IMPRINT",FACE,{"disambiguationData":[TD([[makeQuery(id+"F0.imprint","IMPRINT",EDGE,{"derivedFrom":subQ0}),1.0]])]});}
            var Q74;
            {var subQ0=sQuery(id+"F0.wireOp",EDGE,"E6.2.41.0");Q74=makeQuery(id+"F0.imprint","IMPRINT",FACE,{"disambiguationData":[TD([[makeQuery(id+"F0.imprint","IMPRINT",EDGE,{"derivedFrom":subQ0}),1.0]])]});}
            var Q75;
            {var subQ0=sQuery(id+"F0.wireOp",EDGE,"E6.2.42.0");Q75=makeQuery(id+"F0.imprint","IMPRINT",FACE,{"disambiguationData":[TD([[makeQuery(id+"F0.imprint","IMPRINT",EDGE,{"derivedFrom":subQ0}),1.0]])]});}
            extrude(context, id + "F1", {"entities" : qUnion([Q0, Q1, Q2, Q3, Q4, Q5, Q6, Q7, Q8, Q9, Q10, Q11, Q12, Q13, Q14, Q15, Q16, Q17, Q18, Q19, Q20, Q21, Q22, Q23, Q24, Q25, Q26, Q27, Q28, Q29, Q30, Q31, Q32, Q33, Q34, Q35, Q36, Q37, Q38, Q39, Q40, Q41, Q42, Q43, Q44, Q45, Q46, Q47, Q48, Q49, Q50, Q51, Q52, Q53, Q54, Q55, Q56, Q57, Q58, Q59, Q60, Q61, Q62, Q63, Q64, Q65, Q66, Q67, Q68, Q69, Q70, Q71, Q72, Q73, Q74, Q75]), "depth" : 15 * mm, "offsetDistance" : 25 * mm});
        }
        {
            var Q0;
            Q0=makeQuery(id+"F0.imprint","IMPRINT",FACE,{"disambiguationData":[TD([[makeQuery(id+"F0.imprint","IMPRINT",EDGE,{"derivedFrom":sQuery(id+"F0.wireOp",EDGE,"E1")}),-1.0]])]});
            extrude(context, id + "F2", {"entities" : qUnion([Q0]), "operationType" : NewBodyOperationType.ADD, "depth" : 1 * mm, "offsetDistance" : 25 * mm});
        }
    });
